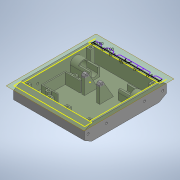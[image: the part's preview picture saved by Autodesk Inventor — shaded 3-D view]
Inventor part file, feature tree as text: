
AUTODESK INVENTOR PART (.ipt)
format: ipt  version: 2020 (Build 240168000, 168)  size: 516,608 bytes
history: native  units: in
note: dims shown in document units (in); Inventor stores cm internally (conversion verified against a paired STEP export)
features: sketch x15, projected_geometry x15, extrude x14, mirror x4, plane x2
ambient origin geometry x8: Origin, YZ Plane, XZ Plane, XY Plane, X Axis, Y Axis, Z Axis, Center Point
bodies: Solid1 (feature_tree)
feature tree (50):
  extrude  "Extrusion1"  Depth=5.9055in
  extrude  "Extrusion2"  TaperAngle=0.0deg  [1 undecoded]
  extrude  "Extrusion3"  Depth=1.063in
  extrude  "Extrusion4"  Depth=0.315in
  extrude  "Extrusion5"  TaperAngle=0.0deg  [1 undecoded]
  extrude  "Extrusion6"  Depth=0.5906in
  mirror  "Mirror1"
  extrude  "Extrusion7"  Depth=0.0787in
  mirror  "Mirror2"
  extrude  "Extrusion8"  Depth=0.6102in
  mirror  "Mirror3"
  plane  "Work Plane1"
  extrude  "Extrusion9"  Depth=0.7874in TaperAngle=0.0deg
  mirror  "Mirror4"
  extrude  "Extrusion10"  Depth=6.063in TaperAngle=0.0deg
  extrude  "Extrusion11"  Depth=0.1575in
  extrude  "Extrusion12"  TaperAngle=0.0deg  [1 undecoded]
  extrude  "Extrusion13"  Depth=0.2756in
  extrude  "Extrusion14"  Depth=0.4331in
  plane  "Work Plane2"
  sketch  "Sketch18"  dims[d34=0.122in d38=2.7559in d40=0.061in d41=0.0909in d42=0.2362in d43=0.0in d44=60.0deg d45=0.0787in d46=0.315in d48=0.993in d49=0.0in d51=0.1575in d52=0.1575in d53=0.2756in d54=0.0in d55=0.4724in d56=1.1614in d57=1.5748in d58=1.5945in d59=0.0787in d60=0.0787in d62=0.315in d63=0.7677in d64=0.0in d65=0.1575in d66=0.1575in d67=0.2756in d68=0.0in d69=0.8268in d70=0.2953in d71=0.0394in d72=0.0in d76=0.1575in d77=120.0deg d79=0.1969in d80=0.1969in d81=0.1969in d82=0.1969in d83=0.1969in d85=120.0deg]
  sketch  "Sketch1"  dims[d0=1.1811in d1=5.9055in]
  sketch  "Sketch2"  dims[d2=5.1181in d3=0.0in]
  projected_geometry  "Projected Loop1"
  sketch  "Sketch3"  dims[d4=0.1575in d5=1.063in]
  projected_geometry  "Projected Loop2"
  projected_geometry  "Projected Loop3"
  sketch  "Sketch4"  dims[d6=0.0in d8=0.315in]
  sketch  "Sketch5"  dims[d10=0.993in d11=0.0in]
  projected_geometry  "Projected Loop4"
  sketch  "Sketch6"  dims[d12=0.6496in d13=0.5906in]
  sketch  "Sketch7"  dims[d14=1.5748in d15=0.0787in]
  sketch  "Sketch9"  dims[d16=0.5512in d17=0.0in d18=0.6102in]
  sketch  "Sketch10"  dims[d19=0.4803in d20=0.7874in d21=0.0in]
  sketch  "Sketch12"  dims[d22=0.1654in d23=6.063in d24=0.0in]
  projected_geometry  "Projected Loop6"
  projected_geometry  "Projected Loop7"
  projected_geometry  "Projected Loop8"
  sketch  "Sketch13"  dims[d25=0.5114in d26=0.1575in]
  projected_geometry  "Projected Loop9"
  projected_geometry  "Projected Loop10"
  projected_geometry  "Projected Loop11"
  projected_geometry  "Projected Loop12"
  projected_geometry  "Projected Loop13"
  projected_geometry  "Projected Loop14"
  sketch  "Sketch14"  dims[d27=1.5748in d28=0.0in d29=0.0in]
  sketch  "Sketch15"  dims[d30=0.1575in d31=0.2756in]
  projected_geometry  "Projected Loop15"
  sketch  "Sketch16"  dims[d32=0.0in d33=0.4331in]
  projected_geometry  "Projected Loop18"
note: 3 required parameter values undecoded (feature->parameter linkage not recoverable at this tier; creation-order binding heuristic only, values carry confidence <= 0.55)
